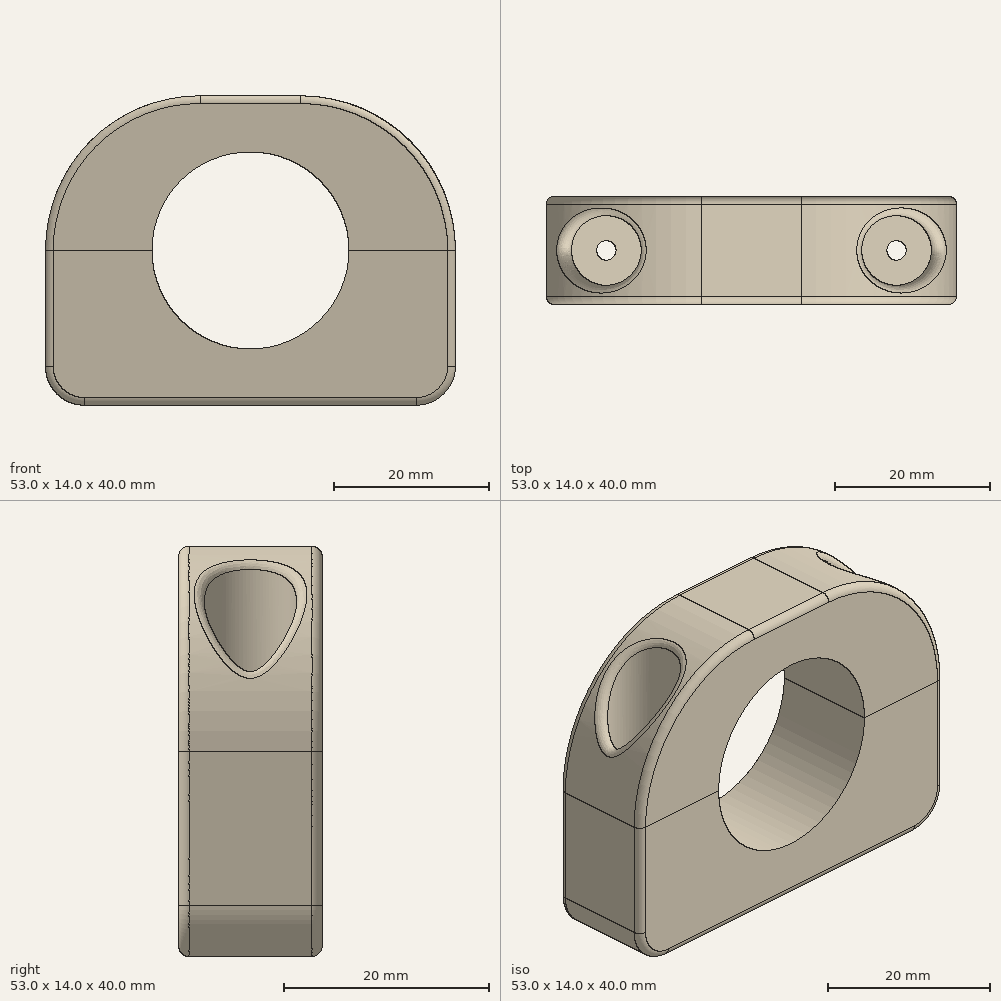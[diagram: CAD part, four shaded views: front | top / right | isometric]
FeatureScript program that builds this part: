
annotation { "Feature Type Name" : "Feature", "Feature Type Description" : "" }
export const myFeature = defineFeature(function(context is Context, id is Id, definition is map)
    precondition{}
    {
        {
            var Q0;
            Q0=qCreatedBy(makeId("Top.planeOp"),FACE);
            var sketch = newSketch(context, id + "F0", { "sketchPlane" : qUnion([Q0])});
            skLineSegment(sketch, "E0.bottom", {"start": v(26.5, -7) * mm, "end": v(-26.5, -7) * mm});
            skLineSegment(sketch, "E0.top", {"start": v(26.5, 7) * mm, "end": v(-26.5, 7) * mm});
            skLineSegment(sketch, "E0.left", {"start": v(26.5, -7) * mm, "end": v(26.5, 7) * mm});
            skLineSegment(sketch, "E0.right", {"start": v(-26.5, -7) * mm, "end": v(-26.5, 7) * mm});
            skPoint(sketch, "E0.middle", {"position": v(0, 0) * mm});
            skSolve(sketch);
        }
        {
            var Q0;
            Q0=qSketchRegion(id+"F0",true);
            extrude(context, id + "F1", {"entities" : qUnion([Q0]), "oppositeDirection" : true, "depth" : 20 * mm, "offsetDistance" : 25 * mm});
        }
        {
            var Q0;
            Q0=qCreatedBy(makeId("Top.planeOp"),FACE);
            var sketch = newSketch(context, id + "F2", { "sketchPlane" : qUnion([Q0])});
            skLineSegment(sketch, "E1.bottom", {"start": v(26.5, 7) * mm, "end": v(-26.5, 7) * mm});
            skLineSegment(sketch, "E1.top", {"start": v(26.5, -7) * mm, "end": v(-26.5, -7) * mm});
            skLineSegment(sketch, "E1.left", {"start": v(26.5, 7) * mm, "end": v(26.5, -7) * mm});
            skLineSegment(sketch, "E1.right", {"start": v(-26.5, 7) * mm, "end": v(-26.5, -7) * mm});
            skPoint(sketch, "E1.middle", {"position": v(0, 0) * mm});
            skSolve(sketch);
        }
        {
            var Q0;
            Q0=qSketchRegion(id+"F2",true);
            extrude(context, id + "F3", {"entities" : qUnion([Q0]), "depth" : 20 * mm, "offsetDistance" : 25 * mm});
        }
        {
            var Q0;
            Q0=qCreatedBy(makeId("Front.planeOp"),FACE);
            var sketch = newSketch(context, id + "F4", { "sketchPlane" : qUnion([Q0])});
            skCircle(sketch, "E2", {"center": v(0, 0) * mm, "radius": 12.73 * mm});
            skSolve(sketch);
        }
        {
            var Q0;
            Q0=qSketchRegion(id+"F4",true);
            extrude(context, id + "F5", {"entities" : qUnion([Q0]), "operationType" : NewBodyOperationType.REMOVE, "endBound" : BoundingType.SYMMETRIC, "oppositeDirection" : true, "depth" : 25 * mm, "offsetDistance" : 25 * mm});
        }
        {
            var Q0;
            Q0=makeQuery(id+"F3.opExtrude","CAP_FACE",FACE,{"disambiguationData":[OSD([sQuery(id+"F2.wireOp",EDGE,"E1.bottom"),sQuery(id+"F2.wireOp",EDGE,"E1.top"),sQuery(id+"F2.wireOp",EDGE,"E1.left"),sQuery(id+"F2.wireOp",EDGE,"E1.right")])],"isStart":false});
            var sketch = newSketch(context, id + "F6", { "sketchPlane" : qUnion([Q0])});
            skCircle(sketch, "E3", {"center": v(18.75, 0) * mm, "radius": 1.25 * mm});
            skCircle(sketch, "E4.MirrorC", {"center": v(-18.75, 0) * mm, "radius": 1.25 * mm});
            skSolve(sketch);
        }
        {
            var Q0;
            Q0=qSketchRegion(id+"F6",true);
            extrude(context, id + "F7", {"entities" : qUnion([Q0]), "operationType" : NewBodyOperationType.REMOVE, "endBound" : BoundingType.THROUGH_ALL, "oppositeDirection" : true, "depth" : 35 * mm, "offsetDistance" : 25 * mm});
        }
        {
            var Q0;
            Q0=makeQuery(id+"F3.opExtrude","CAP_FACE",FACE,{"disambiguationData":[OSD([sQuery(id+"F2.wireOp",EDGE,"E1.bottom"),sQuery(id+"F2.wireOp",EDGE,"E1.top"),sQuery(id+"F2.wireOp",EDGE,"E1.left"),sQuery(id+"F2.wireOp",EDGE,"E1.right")])],"isStart":false});
            var sketch = newSketch(context, id + "F8", { "sketchPlane" : qUnion([Q0])});
            skCircle(sketch, "E5", {"center": v(18.75, 0) * mm, "radius": 4.5 * mm});
            skCircle(sketch, "E6.MirrorC", {"center": v(-18.75, 0) * mm, "radius": 4.5 * mm});
            skSolve(sketch);
        }
        {
            var Q0;
            Q0=qSketchRegion(id+"F8",true);
            var Q1;
            {var subQ0=sQuery(id+"F2.wireOp",EDGE,"E1.bottom");var subQ1=sQuery(id+"F2.wireOp",EDGE,"E1.top");var subQ2=sQuery(id+"F2.wireOp",EDGE,"E1.left");Q1=makeQuery(id+"F5.boolean.opBoolean","SPLIT",FACE,{"disambiguationData":[TD([makeQuery(id+"F3.opExtrude","SWEPT_FACE",FACE,{"disambiguationData":[OSD([subQ2])]})])],"derivedFrom":makeQuery(id+"F3.opExtrude","CAP_FACE",FACE,{"disambiguationData":[OSD([subQ0,subQ1,subQ2,sQuery(id+"F2.wireOp",EDGE,"E1.right")])],"isStart":true})});}
            var Q2;
            Q2=makeQuery(id+"F3.opExtrude","SWEPT_BODY",BODY,{"disambiguationData":[OSD([sQuery(id+"F2.wireOp",EDGE,"E1.bottom"),sQuery(id+"F2.wireOp",EDGE,"E1.top"),sQuery(id+"F2.wireOp",EDGE,"E1.left"),sQuery(id+"F2.wireOp",EDGE,"E1.right")])]});
            extrude(context, id + "F9", {"entities" : qUnion([Q0]), "operationType" : NewBodyOperationType.REMOVE, "endBound" : BoundingType.UP_TO_SURFACE, "oppositeDirection" : true, "depth" : 15 * mm, "endBoundEntityFace" : qUnion([Q1]), "endBoundEntityBody" : qUnion([Q2]), "hasOffset" : true, "offsetDistance" : 3 * mm});
        }
        {
            var Q0;
            Q0=makeQuery(id+"F3.opExtrude","CAP_EDGE",EDGE,{"disambiguationData":[OSD([sQuery(id+"F2.wireOp",EDGE,"E1.left")])],"isStart":false});
            var Q1;
            Q1=makeQuery(id+"F3.opExtrude","CAP_EDGE",EDGE,{"disambiguationData":[OSD([sQuery(id+"F2.wireOp",EDGE,"E1.right")])],"isStart":false});
            fillet(context, id + "F10", {"entities" : qUnion([Q0, Q1]), "radius" : 20 * mm, "tangentPropagation" : true, "allowEdgeOverflow" : false});
        }
        {
            var Q0;
            Q0=makeQuery(id+"F1.opExtrude","CAP_FACE",FACE,{"disambiguationData":[OSD([sQuery(id+"F0.wireOp",EDGE,"E0.bottom"),sQuery(id+"F0.wireOp",EDGE,"E0.top"),sQuery(id+"F0.wireOp",EDGE,"E0.left"),sQuery(id+"F0.wireOp",EDGE,"E0.right")])],"isStart":false});
            var sketch = newSketch(context, id + "F11", { "sketchPlane" : qUnion([Q0])});
            skCircle(sketch, "E7", {"center": v(13.25, 0) * mm, "radius": 1.25 * mm});
            skCircle(sketch, "E8.MirrorC", {"center": v(-13.25, 0) * mm, "radius": 1.25 * mm});
            skSolve(sketch);
        }
        {
            var Q0;
            Q0 = qSketchRegion(id + "F11", true);
            extrude(context, id + "F12", {"entities" : qUnion([Q0]), "operationType" : NewBodyOperationType.REMOVE, "oppositeDirection" : true, "depth" : 8 * mm, "offsetDistance" : 25 * mm});
        }
        {
            var Q0;
            Q0=makeQuery(id+"F1.opExtrude","CAP_EDGE",EDGE,{"disambiguationData":[OSD([sQuery(id+"F0.wireOp",EDGE,"E0.right")])],"isStart":false});
            var Q1;
            Q1=makeQuery(id+"F1.opExtrude","CAP_EDGE",EDGE,{"disambiguationData":[OSD([sQuery(id+"F0.wireOp",EDGE,"E0.left")])],"isStart":false});
            fillet(context, id + "F13", {"entities" : qUnion([Q0, Q1]), "tangentPropagation" : true, "radius" : 5 * mm, "defaultsChanged" : false, "vertexSettings" : [], "allowEdgeOverflow" : false});
        }
        {
            var Q0;
            Q0=makeQuery(id+"F1.opExtrude","SWEPT_EDGE",EDGE,{"disambiguationData":[OSD([sQuery(id+"F0.wireOp",EDGE,"E0.bottom"),sQuery(id+"F0.wireOp",EDGE,"E0.right")])]});
            var Q1;
            Q1=makeQuery(id+"F10.opFillet","BLEND_EDGE",EDGE,{"blendedFrom":[makeQuery(id+"F3.opExtrude","CAP_EDGE",EDGE,{"disambiguationData":[OSD([sQuery(id+"F2.wireOp",EDGE,"E1.right")])],"isStart":false}),makeQuery(id+"F3.opExtrude","SWEPT_FACE",FACE,{"disambiguationData":[OSD([sQuery(id+"F2.wireOp",EDGE,"E1.top")])]})],"blendedInto":[makeQuery(id+"F3.opExtrude","SWEPT_FACE",FACE,{"disambiguationData":[OSD([sQuery(id+"F2.wireOp",EDGE,"E1.top")])]})]});
            var Q2;
            Q2=makeQuery(id+"F1.opExtrude","SWEPT_EDGE",EDGE,{"disambiguationData":[OSD([sQuery(id+"F0.wireOp",EDGE,"E0.top"),sQuery(id+"F0.wireOp",EDGE,"E0.right")])]});
            var Q3;
            Q3=makeQuery(id+"F10.opFillet","BLEND_EDGE",EDGE,{"blendedFrom":[makeQuery(id+"F3.opExtrude","CAP_EDGE",EDGE,{"disambiguationData":[OSD([sQuery(id+"F2.wireOp",EDGE,"E1.right")])],"isStart":false}),makeQuery(id+"F3.opExtrude","SWEPT_FACE",FACE,{"disambiguationData":[OSD([sQuery(id+"F2.wireOp",EDGE,"E1.bottom")])]})],"blendedInto":[makeQuery(id+"F3.opExtrude","SWEPT_FACE",FACE,{"disambiguationData":[OSD([sQuery(id+"F2.wireOp",EDGE,"E1.bottom")])]})]});
            var Q4;
            Q4=makeQuery(id+"F10.opFillet","BLEND_EDGE",EDGE,{"blendedFrom":[makeQuery(id+"F3.opExtrude","CAP_EDGE",EDGE,{"disambiguationData":[OSD([sQuery(id+"F2.wireOp",EDGE,"E1.left")])],"isStart":false}),makeQuery(id+"F9.boolean.opBoolean","COPY",FACE,{"derivedFrom":makeQuery(id+"F9.opExtrude","SWEPT_FACE",FACE,{"disambiguationData":[OSD([sQuery(id+"F8.wireOp",EDGE,"E5")])]})})],"blendedInto":[makeQuery(id+"F9.boolean.opBoolean","COPY",FACE,{"derivedFrom":makeQuery(id+"F9.opExtrude","SWEPT_FACE",FACE,{"disambiguationData":[OSD([sQuery(id+"F8.wireOp",EDGE,"E5")])]})})]});
            var Q5;
            Q5=makeQuery(id+"F10.opFillet","BLEND_EDGE",EDGE,{"blendedFrom":[makeQuery(id+"F3.opExtrude","CAP_EDGE",EDGE,{"disambiguationData":[OSD([sQuery(id+"F2.wireOp",EDGE,"E1.right")])],"isStart":false}),makeQuery(id+"F9.boolean.opBoolean","COPY",FACE,{"derivedFrom":makeQuery(id+"F9.opExtrude","SWEPT_FACE",FACE,{"disambiguationData":[OSD([sQuery(id+"F8.wireOp",EDGE,"E6.MirrorC")])]})})],"blendedInto":[makeQuery(id+"F9.boolean.opBoolean","COPY",FACE,{"derivedFrom":makeQuery(id+"F9.opExtrude","SWEPT_FACE",FACE,{"disambiguationData":[OSD([sQuery(id+"F8.wireOp",EDGE,"E6.MirrorC")])]})})]});
            fillet(context, id + "F14", {"entities" : qUnion([Q0, Q1, Q2, Q3, Q4, Q5]), "tangentPropagation" : true, "radius" : 1 * mm, "defaultsChanged" : false, "vertexSettings" : [], "allowEdgeOverflow" : false});
        }
    });
